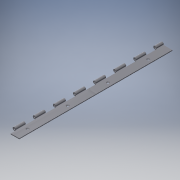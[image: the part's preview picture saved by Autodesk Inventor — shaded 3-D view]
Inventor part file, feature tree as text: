
AUTODESK INVENTOR PART (.ipt)
format: ipt  version: 2016 (Build 200138000, 138)  size: 189,440 bytes
history: native  units: mm
features: sketch x4, extrude x3, pattern_linear x1, hole x1
ambient origin geometry x8: Origin, YZ Plane, XZ Plane, XY Plane, X Axis, Y Axis, Z Axis, Center Point
bodies: Solid1 (feature_tree)
feature tree (9):
  extrude  "Extrusion1"  Depth=3.0mm
  extrude  "Extrusion2"  Depth=20.0mm
  pattern_linear  "Rectangular Pattern1"  Count1=180 Spacing1=0.0mm
  extrude  "Extrusion3"  Depth=80.0mm
  hole  "Hole1"  [1 undecoded]
  sketch  "Sketch2"  dims[d0=1.5mm d1=1.5mm d2=20.0mm d3=3.0mm d4=4.712389mm]
  sketch  "Sketch3"  dims[d5=304.8mm d6=0.0mm d8=20.0mm]
  sketch  "Sketch4"  dims[d9=6.0mm d10=1800.0mm d11=0.0mm]
  sketch  "Sketch5"  dims[d12=250.0mm d14=40.0mm d15=8.0mm d16=3.0mm d17=6.0mm d18=6.0mm d19=2.0mm d20=90.0deg d21=8.0mm d22=20.594885mm d24=30.0mm d25=10.0mm d26=6.0mm d27=10.0mm d28=0.0mm d29=40.0mm d30=80.0mm d31=80.0mm d32=80.0mm d33=80.0mm d34=80.0mm d35=80.0mm d36=80.0mm d37=80.0mm d38=80.0mm d39=80.0mm d40=80.0mm]
note: 1 required parameter value undecoded (feature->parameter linkage not recoverable at this tier; creation-order binding heuristic only, values carry confidence <= 0.55)
